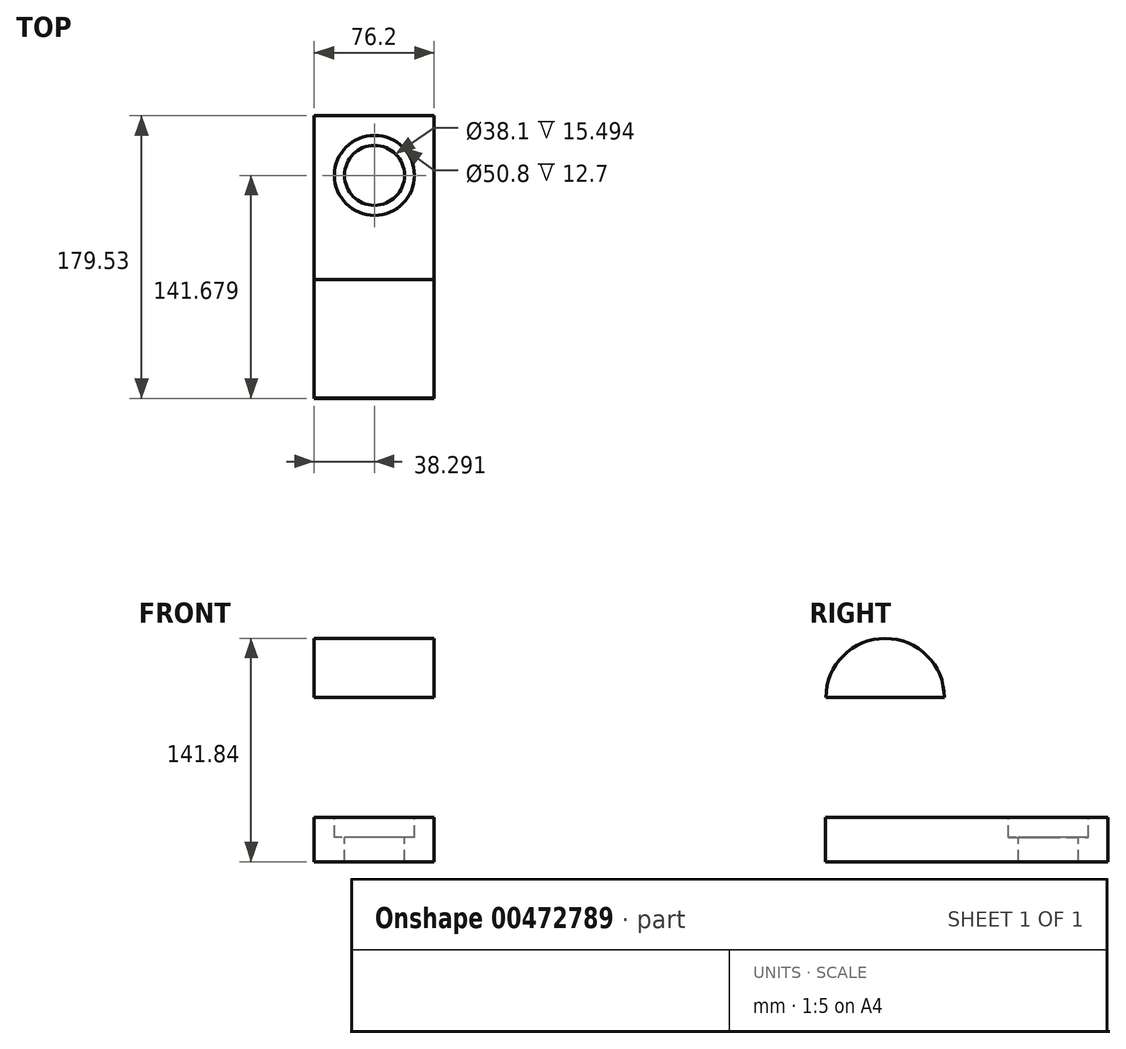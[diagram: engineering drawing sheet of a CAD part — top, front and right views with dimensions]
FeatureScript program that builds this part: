
annotation { "Feature Type Name" : "Feature", "Feature Type Description" : "" }
export const myFeature = defineFeature(function(context is Context, id is Id, definition is map)
    precondition{}
    {
        {
            var Q0;
            Q0=qCreatedBy(makeId("Right.planeOp"),FACE);
            var sketch = newSketch(context, id + "F0", { "sketchPlane" : qUnion([Q0])});
            skLineSegment(sketch, "E0.bottom", {"start": v(-75.9, 0) * mm, "end": v(103.63, 0) * mm});
            skLineSegment(sketch, "E0.top", {"start": v(-75.9, -28.2) * mm, "end": v(103.63, -28.2) * mm});
            skLineSegment(sketch, "E0.left", {"start": v(-75.9, 0) * mm, "end": v(-75.9, -28.2) * mm});
            skLineSegment(sketch, "E0.right", {"start": v(103.63, 0) * mm, "end": v(103.63, -28.2) * mm});
            skLineSegment(sketch, "E1.bottom", {"start": v(-75.9, 0) * mm, "end": v(0, 0) * mm});
            skLineSegment(sketch, "E1.top", {"start": v(-75.9, 76.05) * mm, "end": v(0, 76.05) * mm});
            skLineSegment(sketch, "E1.left", {"start": v(-75.9, 0) * mm, "end": v(-75.9, 76.05) * mm});
            skLineSegment(sketch, "E1.right", {"start": v(0, 0) * mm, "end": v(0, 76.05) * mm});
            skArc(sketch, "E2", {"start": v(-0.34, 76.05) * mm, "mid": v(-37.95, 113.65) * mm, "end": v(-75.55, 76.05) * mm});
            skSolve(sketch);
        }
        {
            var Q0;
            {var subQ0=sQuery(id+"F0.wireOp",EDGE,"E2");Q0=makeQuery(id+"F0.imprint","IMPRINT",FACE,{"disambiguationData":[TD([[makeQuery(id+"F0.imprint","IMPRINT",EDGE,{"derivedFrom":subQ0}),1.0]])]});}
            var Q1;
            Q1=makeQuery(id+"F0.imprint","IMPRINT",FACE,{"disambiguationData":[TD([[makeQuery(id+"F0.imprint","IMPRINT",EDGE,{"derivedFrom":sQuery(id+"F0.wireOp",EDGE,"E1.bottom")}),1.0]])]});
            var Q2;
            Q2=makeQuery(id+"F0.imprint","IMPRINT",FACE,{"disambiguationData":[TD([[makeQuery(id+"F0.imprint","IMPRINT",EDGE,{"derivedFrom":sQuery(id+"F0.wireOp",EDGE,"E0.bottom")}),-1.0]])]});
            extrude(context, id + "F1", {"entities" : qUnion([Q0, Q1, Q2]), "depth" : 76.2 * mm});
        }
        {
            var Q0;
            Q0=qCreatedBy(makeId("Top.planeOp"),FACE);
            var sketch = newSketch(context, id + "F2", { "sketchPlane" : qUnion([Q0])});
            skPoint(sketch, "E3", {"position": v(38.3, 65.78) * mm});
            skPoint(sketch, "E4.end.orphan", {"position": v(76.58, 65.78) * mm});
            skPoint(sketch, "E5.end.orphan", {"position": v(0, 65.78) * mm});
            skPoint(sketch, "E5.start.orphan", {"position": v(0, 103.65) * mm});
            skSolve(sketch);
        }
        {
            var Q0;
            Q0=sQuery(id+"F2.wireOp",VERTEX,"E3");
            var Q1;
            Q1=makeQuery(id+"F1.opExtrude","SWEPT_BODY",BODY,{"disambiguationData":[OSD([sQuery(id+"F0.wireOp",EDGE,"E0.bottom"),sQuery(id+"F0.wireOp",EDGE,"E0.top"),sQuery(id+"F0.wireOp",EDGE,"E0.left"),sQuery(id+"F0.wireOp",EDGE,"E0.right"),sQuery(id+"F0.wireOp",EDGE,"E1.top"),sQuery(id+"F0.wireOp",EDGE,"E1.left"),sQuery(id+"F0.wireOp",EDGE,"E1.right"),sQuery(id+"F0.wireOp",EDGE,"E2")])]});
            hole(context, id + "F3", {"style" : HoleStyle.C_BORE, "endStyle" : HoleEndStyle.BLIND, "holeDiameter" : 38.1 * mm, "cBoreDiameter" : 50.8 * mm, "cBoreDepth" : 12.7 * mm, "holeDepth" : 38.1 * mm, "isTappedThrough" : true, "tappedDepth" : 12.7 * mm, "tapClearance" : 3, "locations" : qUnion([Q0]), "scope" : qUnion([Q1])});
        }
        {
            var Q0;
            Q0=sQuery(id+"F0.wireOp",VERTEX,"E2.center");
            var Q1;
            Q1=makeQuery(id+"F1.opExtrude","SWEPT_BODY",BODY,{"disambiguationData":[OSD([sQuery(id+"F0.wireOp",EDGE,"E0.bottom"),sQuery(id+"F0.wireOp",EDGE,"E0.top"),sQuery(id+"F0.wireOp",EDGE,"E0.left"),sQuery(id+"F0.wireOp",EDGE,"E0.right"),sQuery(id+"F0.wireOp",EDGE,"E1.top"),sQuery(id+"F0.wireOp",EDGE,"E1.left"),sQuery(id+"F0.wireOp",EDGE,"E1.right"),sQuery(id+"F0.wireOp",EDGE,"E2")])]});
            hole(context, id + "F4", {"style" : HoleStyle.C_BORE, "endStyle" : HoleEndStyle.BLIND, "oppositeDirection" : true, "holeDiameter" : 41.15 * mm, "cBoreDiameter" : 50.8 * mm, "cBoreDepth" : 12.7 * mm, "holeDepth" : 76.2 * mm, "isTappedThrough" : true, "tappedDepth" : 12.7 * mm, "tapClearance" : 3, "locations" : qUnion([Q0]), "scope" : qUnion([Q1])});
        }
    });
